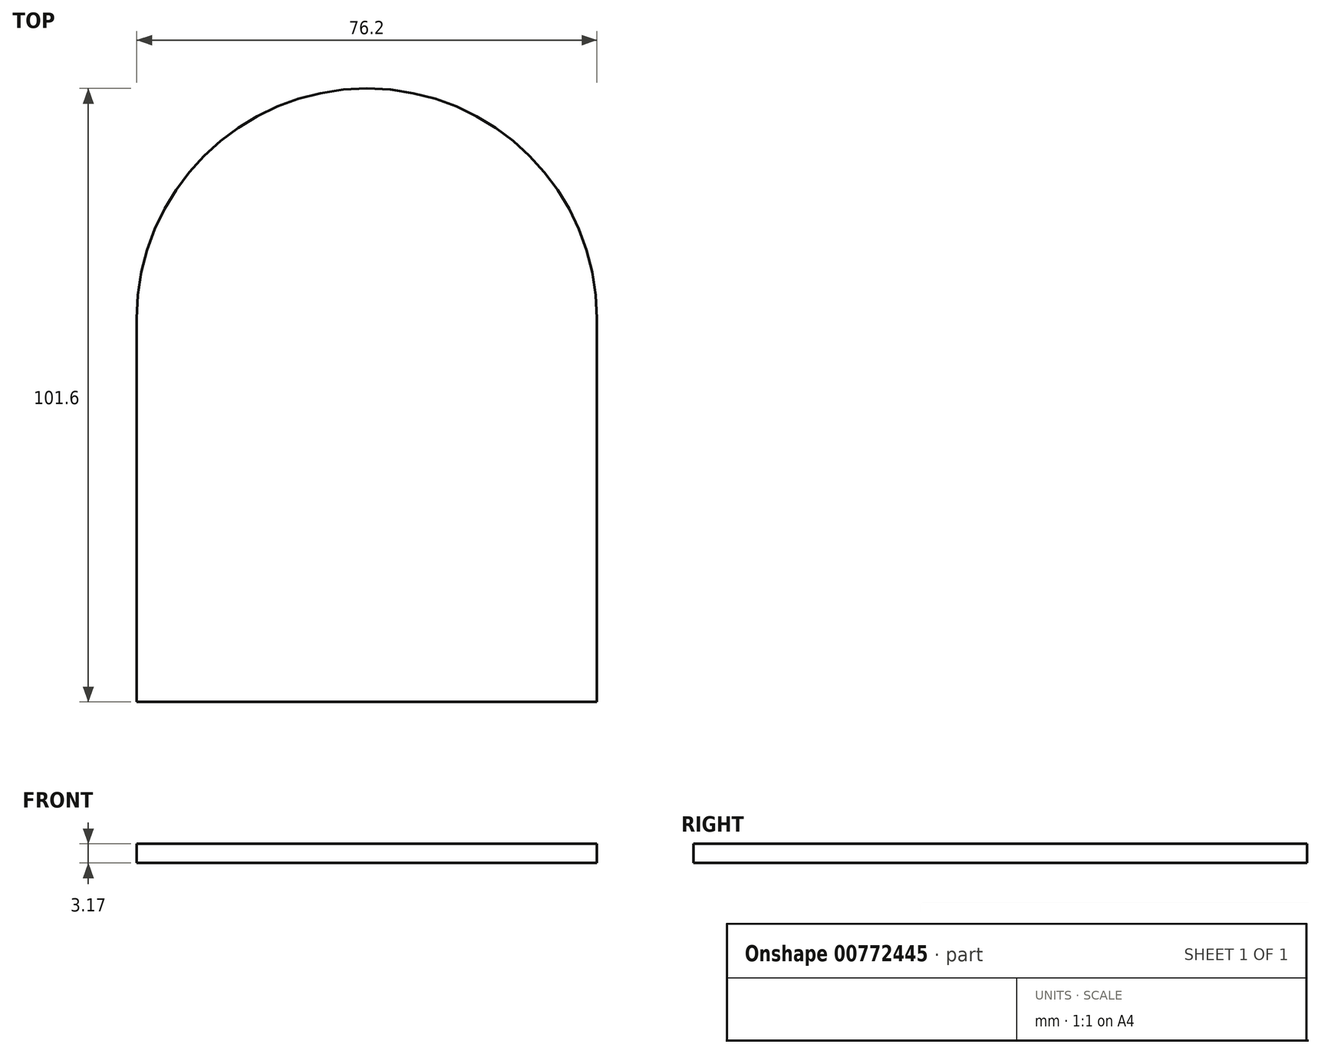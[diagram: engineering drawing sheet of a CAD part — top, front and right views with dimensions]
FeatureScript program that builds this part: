
annotation { "Feature Type Name" : "Feature", "Feature Type Description" : "" }
export const myFeature = defineFeature(function(context is Context, id is Id, definition is map)
    precondition{}
    {
        {
            var Q0;
            Q0=qCreatedBy(makeId("Top.planeOp"),FACE);
            var sketch = newSketch(context, id + "F0", { "sketchPlane" : qUnion([Q0])});
            skArc(sketch, "E0", {"start": v(38.1, 0) * mm, "mid": v(0, 38.1) * mm, "end": v(-38.1, 0) * mm});
            skLineSegment(sketch, "E1", {"start": v(-38.1, 0) * mm, "end": v(-38.1, -63.5) * mm});
            skLineSegment(sketch, "E2", {"start": v(38.1, 0) * mm, "end": v(38.1, -63.5) * mm});
            skLineSegment(sketch, "E3", {"start": v(38.1, -63.5) * mm, "end": v(-38.1, -63.5) * mm});
            skArc(sketch, "E4.0", {"start": v(34.93, 0) * mm, "mid": v(0, 34.93) * mm, "end": v(-34.93, 0) * mm});
            skLineSegment(sketch, "E5.0", {"start": v(34.93, 0) * mm, "end": v(34.93, -60.32) * mm});
            skLineSegment(sketch, "E5.1", {"start": v(34.93, -60.32) * mm, "end": v(-34.93, -60.32) * mm});
            skLineSegment(sketch, "E5.2", {"start": v(-34.93, 0) * mm, "end": v(-34.93, -60.32) * mm});
            skSolve(sketch);
        }
        {
            var Q0;
            Q0=makeQuery(id+"F0.imprint","IMPRINT",FACE,{"disambiguationData":[TD([[makeQuery(id+"F0.imprint","IMPRINT",EDGE,{"derivedFrom":sQuery(id+"F0.wireOp",EDGE,"E4.0")}),1.0]])]});
            extrude(context, id + "F1", {"entities" : qUnion([Q0]), "depth" : 3.17 * mm, "offsetDistance" : 25.4 * mm});
        }
        {
            var Q0;
            Q0=makeQuery(id+"F0.imprint","IMPRINT",FACE,{"disambiguationData":[TD([[makeQuery(id+"F0.imprint","IMPRINT",EDGE,{"derivedFrom":sQuery(id+"F0.wireOp",EDGE,"E0")}),1.0]])]});
            extrude(context, id + "F2", {"entities" : qUnion([Q0]), "operationType" : NewBodyOperationType.ADD, "depth" : 3.17 * mm, "offsetDistance" : 25.4 * mm});
        }
    });
